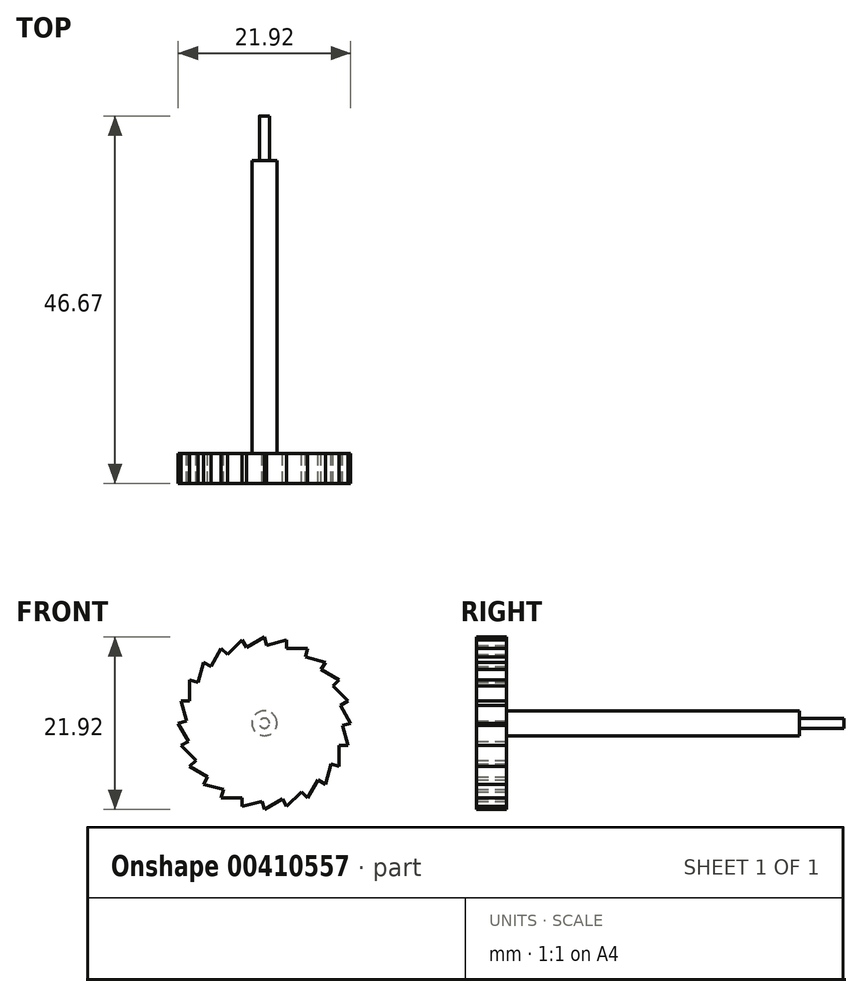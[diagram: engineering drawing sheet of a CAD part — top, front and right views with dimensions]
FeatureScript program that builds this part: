
annotation { "Feature Type Name" : "Feature", "Feature Type Description" : "" }
export const myFeature = defineFeature(function(context is Context, id is Id, definition is map)
    precondition{}
    {
        {
            var Q0;
            Q0=qCreatedBy(makeId("Front.planeOp"),FACE);
            var sketch = newSketch(context, id + "F0", { "sketchPlane" : qUnion([Q0])});
            skLineSegment(sketch, "E0", {"start": v(0, 0) * mm, "end": v(0, 10.96) * mm, "construction": true});
            skLineSegment(sketch, "E1", {"start": v(0, 0) * mm, "end": v(-2.84, 10.59) * mm, "construction": true});
            skCircle(sketch, "E2", {"center": v(0, 0) * mm, "radius": 10.96 * mm, "construction": true});
            skLineSegment(sketch, "E3", {"start": v(0, 10.96) * mm, "end": v(-2.29, 9.64) * mm});
            skLineSegment(sketch, "E4", {"start": v(-2.29, 9.64) * mm, "end": v(-2.84, 10.59) * mm});
            skLineSegment(sketch, "E5", {"start": v(0, 10.96) * mm, "end": v(-2.55, 10.96) * mm, "construction": true});
            skLineSegment(sketch, "E6.1.0", {"start": v(0.28, 9.9) * mm, "end": v(0, 10.96) * mm});
            skLineSegment(sketch, "E6.1.1", {"start": v(2.84, 10.59) * mm, "end": v(0.28, 9.9) * mm});
            skLineSegment(sketch, "E6.2.0", {"start": v(2.84, 9.5) * mm, "end": v(2.84, 10.59) * mm});
            skLineSegment(sketch, "E6.2.1", {"start": v(5.48, 9.5) * mm, "end": v(2.84, 9.5) * mm});
            skLineSegment(sketch, "E6.3.0", {"start": v(5.2, 8.43) * mm, "end": v(5.48, 9.5) * mm});
            skLineSegment(sketch, "E6.3.1", {"start": v(7.75, 7.75) * mm, "end": v(5.2, 8.43) * mm});
            skLineSegment(sketch, "E6.4.0", {"start": v(7.2, 6.8) * mm, "end": v(7.75, 7.75) * mm});
            skLineSegment(sketch, "E6.4.1", {"start": v(9.5, 5.48) * mm, "end": v(7.2, 6.8) * mm});
            skLineSegment(sketch, "E6.5.0", {"start": v(8.72, 4.7) * mm, "end": v(9.5, 5.48) * mm});
            skLineSegment(sketch, "E6.5.1", {"start": v(10.59, 2.84) * mm, "end": v(8.72, 4.7) * mm});
            skLineSegment(sketch, "E6.6.0", {"start": v(9.64, 2.29) * mm, "end": v(10.59, 2.84) * mm});
            skLineSegment(sketch, "E6.6.1", {"start": v(10.96, 0) * mm, "end": v(9.64, 2.29) * mm});
            skLineSegment(sketch, "E6.7.0", {"start": v(9.9, -0.28) * mm, "end": v(10.96, 0) * mm});
            skLineSegment(sketch, "E6.7.1", {"start": v(10.59, -2.84) * mm, "end": v(9.9, -0.28) * mm});
            skLineSegment(sketch, "E6.8.0", {"start": v(9.5, -2.84) * mm, "end": v(10.59, -2.84) * mm});
            skLineSegment(sketch, "E6.8.1", {"start": v(9.5, -5.48) * mm, "end": v(9.5, -2.84) * mm});
            skLineSegment(sketch, "E6.9.0", {"start": v(8.43, -5.2) * mm, "end": v(9.5, -5.48) * mm});
            skLineSegment(sketch, "E6.9.1", {"start": v(7.75, -7.75) * mm, "end": v(8.43, -5.2) * mm});
            skLineSegment(sketch, "E6.10.0", {"start": v(6.8, -7.2) * mm, "end": v(7.75, -7.75) * mm});
            skLineSegment(sketch, "E6.10.1", {"start": v(5.48, -9.5) * mm, "end": v(6.8, -7.2) * mm});
            skLineSegment(sketch, "E6.11.0", {"start": v(4.7, -8.72) * mm, "end": v(5.48, -9.5) * mm});
            skLineSegment(sketch, "E6.11.1", {"start": v(2.84, -10.59) * mm, "end": v(4.7, -8.72) * mm});
            skLineSegment(sketch, "E6.12.0", {"start": v(2.29, -9.64) * mm, "end": v(2.84, -10.59) * mm});
            skLineSegment(sketch, "E6.12.1", {"start": v(0, -10.96) * mm, "end": v(2.29, -9.64) * mm});
            skLineSegment(sketch, "E6.13.0", {"start": v(-0.28, -9.9) * mm, "end": v(0, -10.96) * mm});
            skLineSegment(sketch, "E6.13.1", {"start": v(-2.84, -10.59) * mm, "end": v(-0.28, -9.9) * mm});
            skLineSegment(sketch, "E6.14.0", {"start": v(-2.84, -9.5) * mm, "end": v(-2.84, -10.59) * mm});
            skLineSegment(sketch, "E6.14.1", {"start": v(-5.48, -9.5) * mm, "end": v(-2.84, -9.5) * mm});
            skLineSegment(sketch, "E6.15.0", {"start": v(-5.2, -8.43) * mm, "end": v(-5.48, -9.5) * mm});
            skLineSegment(sketch, "E6.15.1", {"start": v(-7.75, -7.75) * mm, "end": v(-5.2, -8.43) * mm});
            skLineSegment(sketch, "E6.16.0", {"start": v(-7.2, -6.8) * mm, "end": v(-7.75, -7.75) * mm});
            skLineSegment(sketch, "E6.16.1", {"start": v(-9.5, -5.48) * mm, "end": v(-7.2, -6.8) * mm});
            skLineSegment(sketch, "E6.17.0", {"start": v(-8.72, -4.7) * mm, "end": v(-9.5, -5.48) * mm});
            skLineSegment(sketch, "E6.17.1", {"start": v(-10.59, -2.84) * mm, "end": v(-8.72, -4.7) * mm});
            skLineSegment(sketch, "E6.18.0", {"start": v(-9.64, -2.29) * mm, "end": v(-10.59, -2.84) * mm});
            skLineSegment(sketch, "E6.18.1", {"start": v(-10.96, 0) * mm, "end": v(-9.64, -2.29) * mm});
            skLineSegment(sketch, "E6.19.0", {"start": v(-9.9, 0.28) * mm, "end": v(-10.96, 0) * mm});
            skLineSegment(sketch, "E6.19.1", {"start": v(-10.59, 2.84) * mm, "end": v(-9.9, 0.28) * mm});
            skLineSegment(sketch, "E6.20.0", {"start": v(-9.5, 2.84) * mm, "end": v(-10.59, 2.84) * mm});
            skLineSegment(sketch, "E6.20.1", {"start": v(-9.5, 5.48) * mm, "end": v(-9.5, 2.84) * mm});
            skLineSegment(sketch, "E6.21.0", {"start": v(-8.43, 5.2) * mm, "end": v(-9.5, 5.48) * mm});
            skLineSegment(sketch, "E6.21.1", {"start": v(-7.75, 7.75) * mm, "end": v(-8.43, 5.2) * mm});
            skLineSegment(sketch, "E6.22.0", {"start": v(-6.8, 7.2) * mm, "end": v(-7.75, 7.75) * mm});
            skLineSegment(sketch, "E6.22.1", {"start": v(-5.48, 9.5) * mm, "end": v(-6.8, 7.2) * mm});
            skLineSegment(sketch, "E6.23.0", {"start": v(-4.7, 8.72) * mm, "end": v(-5.48, 9.5) * mm});
            skLineSegment(sketch, "E6.23.1", {"start": v(-2.84, 10.59) * mm, "end": v(-4.7, 8.72) * mm});
            skLineSegment(sketch, "E6.anchor1", {"start": v(0, 0) * mm, "end": v(-2.29, 9.64) * mm, "construction": true});
            skLineSegment(sketch, "E6.anchor2", {"start": v(0, 0) * mm, "end": v(-2.29, 9.64) * mm, "construction": true});
            skSolve(sketch);
        }
        {
            var Q0;
            Q0 = qSketchRegion(id + "F0", true);
            extrude(context, id + "F1", {"entities" : qUnion([Q0]), "offsetDistance" : 25.4 * mm, "depth" : 3.8 * mm});
        }
        {
            var Q0;
            Q0=qCreatedBy(makeId("Front.planeOp"),FACE);
            var sketch = newSketch(context, id + "F2", { "sketchPlane" : qUnion([Q0])});
            skCircle(sketch, "E7", {"center": v(0, 0) * mm, "radius": 1.59 * mm});
            skSolve(sketch);
        }
        {
            var Q0;
            Q0 = qSketchRegion(id + "F2", true);
            extrude(context, id + "F3", {"entities" : qUnion([Q0]), "operationType" : NewBodyOperationType.ADD, "oppositeDirection" : true, "depth" : 37.2 * mm});
        }
        {
            var Q0;
            Q0=makeQuery(id+"F3.opExtrude","CAP_FACE",FACE,{"disambiguationData":[OSD([sQuery(id+"F2.wireOp",EDGE,"E7")])],"isStart":false});
            var sketch = newSketch(context, id + "F4", { "sketchPlane" : qUnion([Q0])});
            skCircle(sketch, "E8", {"center": v(0, 0) * mm, "radius": 0.64 * mm});
            skSolve(sketch);
        }
        {
            var Q0;
            Q0 = qSketchRegion(id + "F4", true);
            extrude(context, id + "F5", {"entities" : qUnion([Q0]), "operationType" : NewBodyOperationType.ADD, "depth" : 5.66 * mm});
        }
    });
